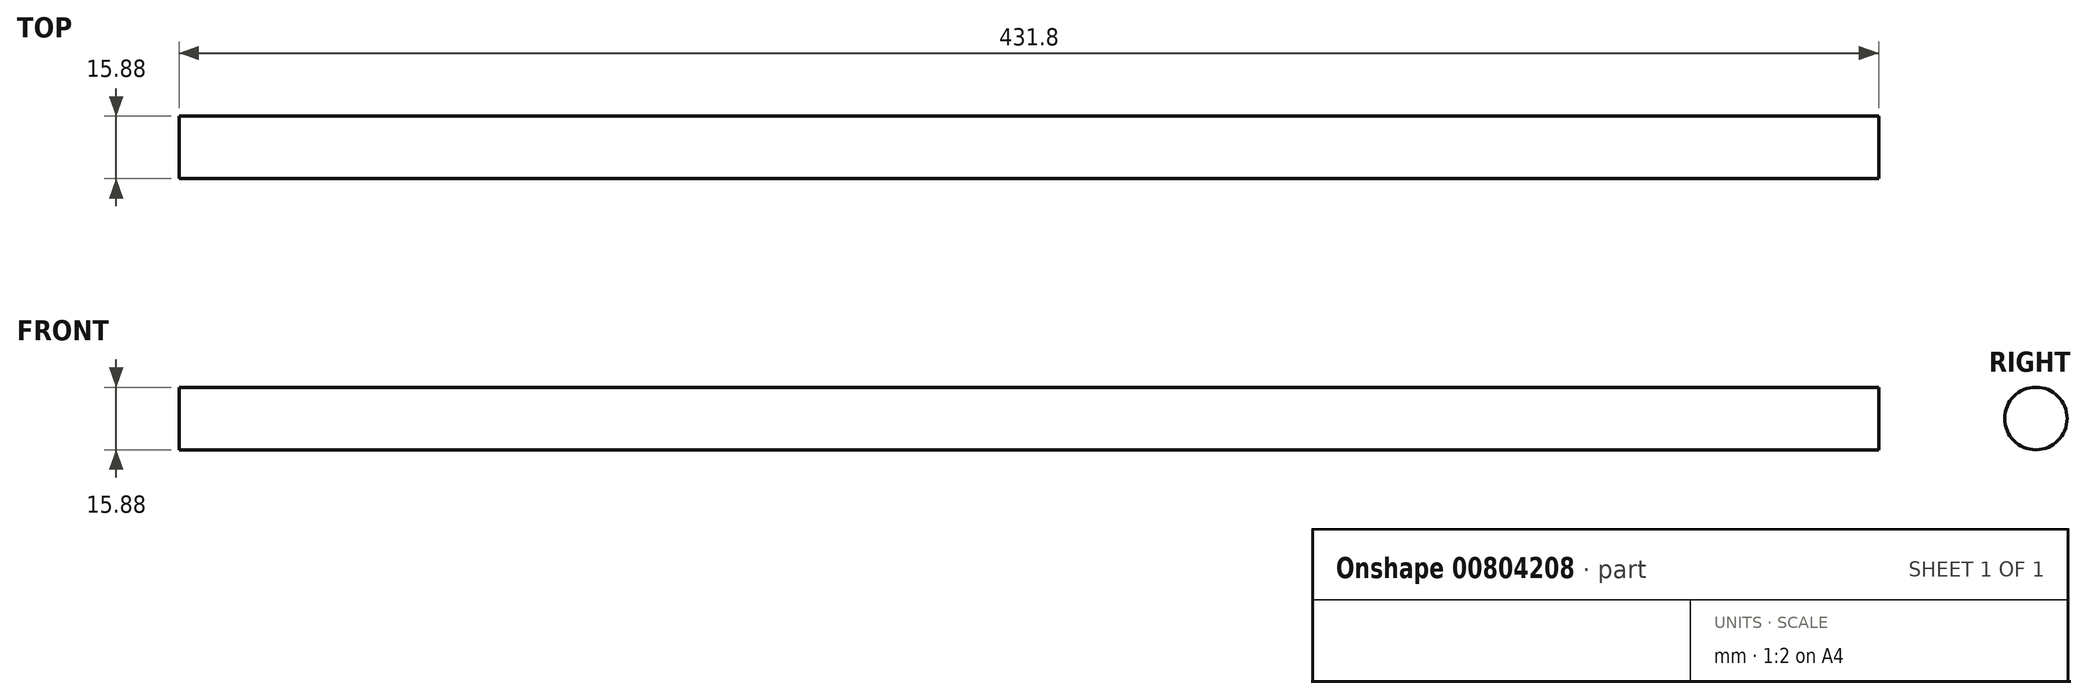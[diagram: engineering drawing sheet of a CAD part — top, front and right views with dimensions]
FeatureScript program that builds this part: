
annotation { "Feature Type Name" : "Feature", "Feature Type Description" : "" }
export const myFeature = defineFeature(function(context is Context, id is Id, definition is map)
    precondition{}
    {
        {
            var Q0;
            Q0=qCreatedBy(makeId("Right.planeOp"),FACE);
            var sketch = newSketch(context, id + "F0", { "sketchPlane" : qUnion([Q0])});
            skCircle(sketch, "E0", {"center": v(0, 0) * mm, "radius": 7.94 * mm});
            skSolve(sketch);
        }
        {
            var Q0;
            Q0=makeQuery(id+"F0.imprint","IMPRINT",FACE,{"disambiguationData":[TD([[makeQuery(id+"F0.imprint","IMPRINT",EDGE,{"derivedFrom":sQuery(id+"F0.wireOp",EDGE,"E0")}),1.0]])]});
            extrude(context, id + "F1", {"entities" : qUnion([Q0]), "depth" : 431.8 * mm, "offsetDistance" : 25.4 * mm});
        }
    });
